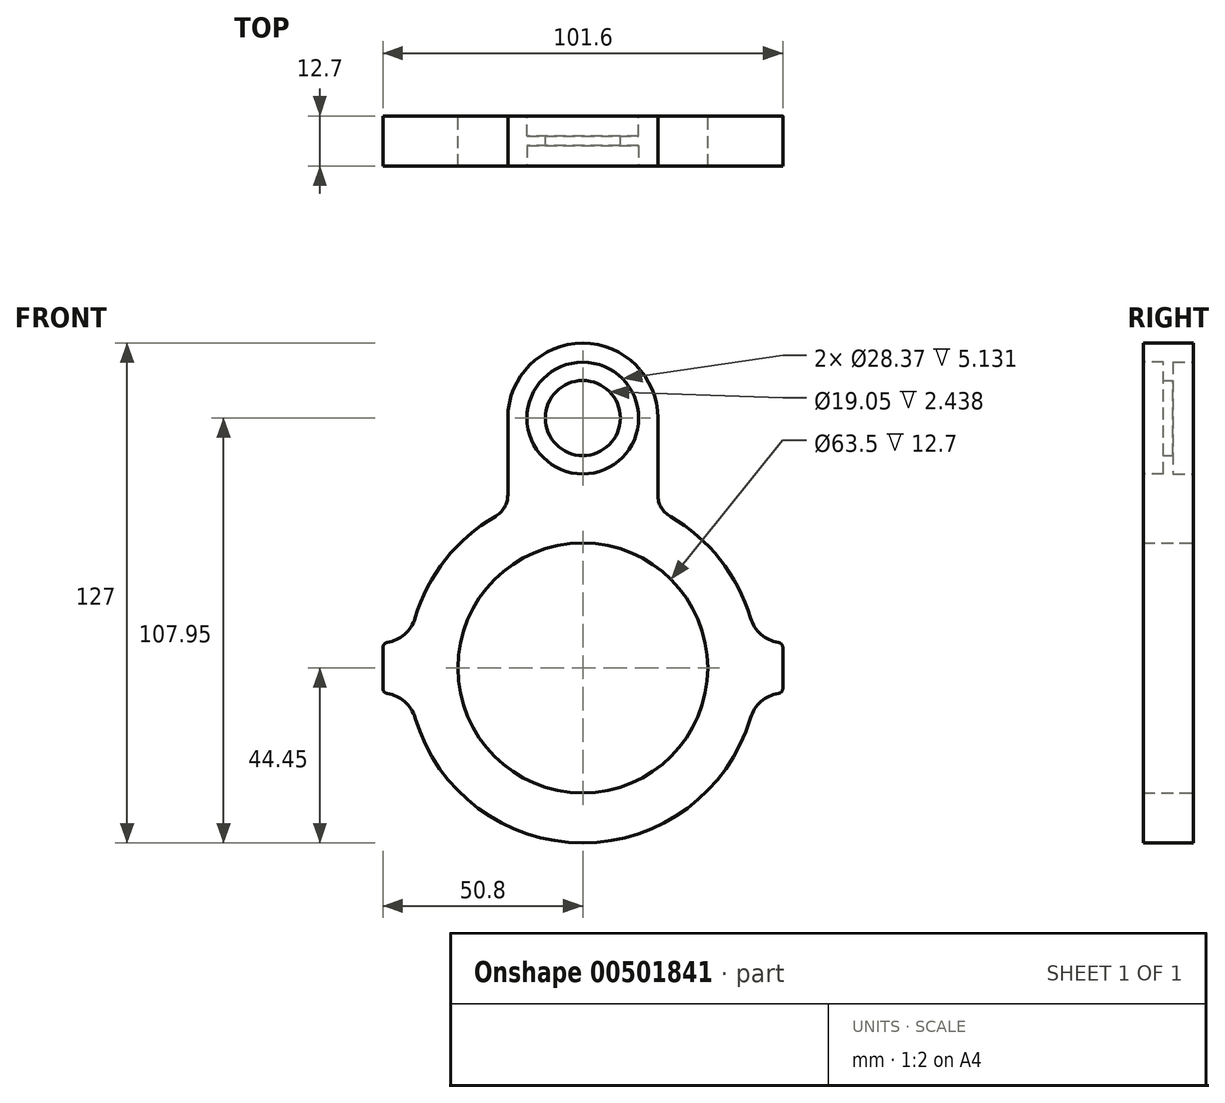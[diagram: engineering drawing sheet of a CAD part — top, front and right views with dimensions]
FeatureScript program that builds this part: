
annotation { "Feature Type Name" : "Feature", "Feature Type Description" : "" }
export const myFeature = defineFeature(function(context is Context, id is Id, definition is map)
    precondition{}
    {
        {
            var Q0;
            Q0=qCreatedBy(makeId("Front.planeOp"),FACE);
            var sketch = newSketch(context, id + "F0", { "sketchPlane" : qUnion([Q0])});
            skLineSegment(sketch, "E0", {"start": v(0, 0) * mm, "end": v(0, -31.75) * mm, "construction": true});
            skLineSegment(sketch, "E1", {"start": v(0, 0) * mm, "end": v(0, 31.75) * mm, "construction": true});
            skCircle(sketch, "E2", {"center": v(0, -31.75) * mm, "radius": 31.75 * mm});
            skCircle(sketch, "E3", {"center": v(0, 31.75) * mm, "radius": 9.53 * mm});
            skArc(sketch, "E4", {"start": v(19.05, 31.75) * mm, "mid": v(0, 50.8) * mm, "end": v(-19.05, 31.75) * mm});
            skArc(sketch, "E5", {"start": v(-35.77, -5.36) * mm, "mid": v(-41.12, -14.87) * mm, "end": v(-44, -25.4) * mm});
            skPoint(sketch, "E6.start.orphan", {"position": v(-44.45, -31.75) * mm});
            skLineSegment(sketch, "E7", {"start": v(0, -31.75) * mm, "end": v(31.75, -31.75) * mm, "construction": true});
            skLineSegment(sketch, "E8", {"start": v(0, -31.75) * mm, "end": v(-50.8, -31.75) * mm, "construction": true});
            skLineSegment(sketch, "E9", {"start": v(-50.8, -25.4) * mm, "end": v(-44, -25.4) * mm});
            skLineSegment(sketch, "E10", {"start": v(-50.8, -38.1) * mm, "end": v(-44, -38.1) * mm});
            skLineSegment(sketch, "E11.trimOffspring", {"start": v(44, -38.1) * mm, "end": v(50.8, -38.1) * mm});
            skLineSegment(sketch, "E12.trimOffspring", {"start": v(44, -25.4) * mm, "end": v(50.8, -25.4) * mm});
            skLineSegment(sketch, "E13", {"start": v(-50.8, -25.4) * mm, "end": v(-50.8, -38.1) * mm});
            skLineSegment(sketch, "E14", {"start": v(50.8, -25.4) * mm, "end": v(50.8, -38.1) * mm});
            skArc(sketch, "E15.trimOffspring", {"start": v(-44, -38.1) * mm, "mid": v(0, -76.2) * mm, "end": v(44, -38.1) * mm});
            skArc(sketch, "E16.trimOffspring", {"start": v(44, -25.4) * mm, "mid": v(41.12, -14.87) * mm, "end": v(35.77, -5.36) * mm});
            skPoint(sketch, "E17.trimOffspring.end.orphan", {"position": v(50.8, -31.75) * mm});
            skPoint(sketch, "E18.MirrorCS.end.orphan", {"position": v(19.05, 31.75) * mm});
            skPoint(sketch, "E18.MirrorCS.start.orphan", {"position": v(35.77, -5.36) * mm});
            skArc(sketch, "E19", {"start": v(35.77, -5.36) * mm, "mid": v(29.62, 1.4) * mm, "end": v(22.23, 6.74) * mm});
            skLineSegment(sketch, "E20", {"start": v(19.05, 31.75) * mm, "end": v(19.05, 12.24) * mm, "construction": true});
            skLineSegment(sketch, "E21", {"start": v(-19.05, 31.75) * mm, "end": v(-19.05, 12.24) * mm, "construction": true});
            skLineSegment(sketch, "E22", {"start": v(19.05, 12.7) * mm, "end": v(-19.05, 12.7) * mm, "construction": true});
            skLineSegment(sketch, "E23", {"start": v(19.05, 31.75) * mm, "end": v(19.05, 12.24) * mm});
            skLineSegment(sketch, "E24", {"start": v(-19.05, 31.75) * mm, "end": v(-19.05, 12.24) * mm});
            skArc(sketch, "E25.trimOffspring", {"start": v(-22.22, 6.74) * mm, "mid": v(-29.62, 1.4) * mm, "end": v(-35.77, -5.36) * mm});
            skPoint(sketch, "E26.newPointB", {"position": v(-19.05, -6.35) * mm});
            skArc(sketch, "E26.filletArc", {"start": v(-22.22, 6.74) * mm, "mid": v(-19.9, 9.07) * mm, "end": v(-19.05, 12.24) * mm});
            skPoint(sketch, "E27.newPointB", {"position": v(19.05, -6.35) * mm});
            skArc(sketch, "E27.filletArc", {"start": v(19.05, 12.24) * mm, "mid": v(19.9, 9.07) * mm, "end": v(22.22, 6.74) * mm});
            skSolve(sketch);
        }
        {
            var Q0;
            Q0 = qSketchRegion(id + "F0", true);
            extrude(context, id + "F1", {"entities" : qUnion([Q0]), "depth" : 12.7 * mm});
        }
        {
            var Q0;
            Q0=makeQuery(id+"F1.opExtrude","SWEPT_EDGE",EDGE,{"disambiguationData":[OSD([sQuery(id+"F0.wireOp",EDGE,"E5"),sQuery(id+"F0.wireOp",EDGE,"E9")])]});
            var Q1;
            Q1=makeQuery(id+"F1.opExtrude","SWEPT_EDGE",EDGE,{"disambiguationData":[OSD([sQuery(id+"F0.wireOp",EDGE,"E12.trimOffspring"),sQuery(id+"F0.wireOp",EDGE,"E16.trimOffspring")])]});
            var Q2;
            Q2=makeQuery(id+"F1.opExtrude","SWEPT_EDGE",EDGE,{"disambiguationData":[OSD([sQuery(id+"F0.wireOp",EDGE,"E10"),sQuery(id+"F0.wireOp",EDGE,"E15.trimOffspring")])]});
            var Q3;
            Q3=makeQuery(id+"F1.opExtrude","SWEPT_EDGE",EDGE,{"disambiguationData":[OSD([sQuery(id+"F0.wireOp",EDGE,"E11.trimOffspring"),sQuery(id+"F0.wireOp",EDGE,"E15.trimOffspring")])]});
            fillet(context, id + "F2", {"entities" : qUnion([Q0, Q1, Q2, Q3]), "radius" : 8.9 * mm, "tangentPropagation" : true, "allowEdgeOverflow" : false});
        }
        {
            var Q0;
            Q0=makeQuery(id+"F2.opFillet","BLEND_EDGE",EDGE,{"blendedFrom":[makeQuery(id+"F1.opExtrude","SWEPT_EDGE",EDGE,{"disambiguationData":[OSD([sQuery(id+"F0.wireOp",EDGE,"E5"),sQuery(id+"F0.wireOp",EDGE,"E9")])]}),makeQuery(id+"F1.opExtrude","SWEPT_FACE",FACE,{"disambiguationData":[OSD([sQuery(id+"F0.wireOp",EDGE,"E13")])]})],"blendedInto":[makeQuery(id+"F1.opExtrude","SWEPT_FACE",FACE,{"disambiguationData":[OSD([sQuery(id+"F0.wireOp",EDGE,"E13")])]})]});
            var Q1;
            Q1=makeQuery(id+"F2.opFillet","BLEND_EDGE",EDGE,{"blendedFrom":[makeQuery(id+"F1.opExtrude","SWEPT_EDGE",EDGE,{"disambiguationData":[OSD([sQuery(id+"F0.wireOp",EDGE,"E10"),sQuery(id+"F0.wireOp",EDGE,"E15.trimOffspring")])]}),makeQuery(id+"F1.opExtrude","SWEPT_FACE",FACE,{"disambiguationData":[OSD([sQuery(id+"F0.wireOp",EDGE,"E13")])]})],"blendedInto":[makeQuery(id+"F1.opExtrude","SWEPT_FACE",FACE,{"disambiguationData":[OSD([sQuery(id+"F0.wireOp",EDGE,"E13")])]})]});
            var Q2;
            Q2=makeQuery(id+"F2.opFillet","BLEND_EDGE",EDGE,{"blendedFrom":[makeQuery(id+"F1.opExtrude","SWEPT_EDGE",EDGE,{"disambiguationData":[OSD([sQuery(id+"F0.wireOp",EDGE,"E12.trimOffspring"),sQuery(id+"F0.wireOp",EDGE,"E16.trimOffspring")])]}),makeQuery(id+"F1.opExtrude","SWEPT_FACE",FACE,{"disambiguationData":[OSD([sQuery(id+"F0.wireOp",EDGE,"E14")])]})],"blendedInto":[makeQuery(id+"F1.opExtrude","SWEPT_FACE",FACE,{"disambiguationData":[OSD([sQuery(id+"F0.wireOp",EDGE,"E14")])]})]});
            var Q3;
            Q3=makeQuery(id+"F2.opFillet","BLEND_EDGE",EDGE,{"blendedFrom":[makeQuery(id+"F1.opExtrude","SWEPT_EDGE",EDGE,{"disambiguationData":[OSD([sQuery(id+"F0.wireOp",EDGE,"E11.trimOffspring"),sQuery(id+"F0.wireOp",EDGE,"E15.trimOffspring")])]}),makeQuery(id+"F1.opExtrude","SWEPT_FACE",FACE,{"disambiguationData":[OSD([sQuery(id+"F0.wireOp",EDGE,"E14")])]})],"blendedInto":[makeQuery(id+"F1.opExtrude","SWEPT_FACE",FACE,{"disambiguationData":[OSD([sQuery(id+"F0.wireOp",EDGE,"E14")])]})]});
            fillet(context, id + "F3", {"entities" : qUnion([Q0, Q1, Q2, Q3]), "radius" : 1.27 * mm, "tangentPropagation" : true, "allowEdgeOverflow" : false});
        }
        {
            var Q0;
            Q0=makeQuery(id+"F1.opExtrude","CAP_FACE",FACE,{"disambiguationData":[OSD([sQuery(id+"F0.wireOp",EDGE,"E2"),sQuery(id+"F0.wireOp",EDGE,"E3"),sQuery(id+"F0.wireOp",EDGE,"E4"),sQuery(id+"F0.wireOp",EDGE,"E5"),sQuery(id+"F0.wireOp",EDGE,"E9"),sQuery(id+"F0.wireOp",EDGE,"E10"),sQuery(id+"F0.wireOp",EDGE,"E11.trimOffspring"),sQuery(id+"F0.wireOp",EDGE,"E12.trimOffspring"),sQuery(id+"F0.wireOp",EDGE,"E13"),sQuery(id+"F0.wireOp",EDGE,"E14"),sQuery(id+"F0.wireOp",EDGE,"E15.trimOffspring"),sQuery(id+"F0.wireOp",EDGE,"E16.trimOffspring"),sQuery(id+"F0.wireOp",EDGE,"E19"),sQuery(id+"F0.wireOp",EDGE,"E23"),sQuery(id+"F0.wireOp",EDGE,"E24"),sQuery(id+"F0.wireOp",EDGE,"E25.trimOffspring"),sQuery(id+"F0.wireOp",EDGE,"E26.filletArc"),sQuery(id+"F0.wireOp",EDGE,"E27.filletArc")])],"isStart":false});
            var sketch = newSketch(context, id + "F4", { "sketchPlane" : qUnion([Q0])});
            skCircle(sketch, "E28", {"center": v(0, 31.75) * mm, "radius": 14.19 * mm});
            skSolve(sketch);
        }
        {
            var Q0;
            Q0=makeQuery(id+"F4.imprint","IMPRINT",FACE,{"disambiguationData":[TD([[makeQuery(id+"F4.imprint","IMPRINT",EDGE,{"derivedFrom":sQuery(id+"F4.wireOp",EDGE,"E28")}),1.0]])]});
            extrude(context, id + "F5", {"entities" : qUnion([Q0]), "operationType" : NewBodyOperationType.REMOVE, "oppositeDirection" : true, "depth" : 5.13 * mm});
        }
        {
            var Q0;
            Q0=makeQuery(id+"F1.opExtrude","CAP_FACE",FACE,{"disambiguationData":[OSD([sQuery(id+"F0.wireOp",EDGE,"E2"),sQuery(id+"F0.wireOp",EDGE,"E3"),sQuery(id+"F0.wireOp",EDGE,"E4"),sQuery(id+"F0.wireOp",EDGE,"E5"),sQuery(id+"F0.wireOp",EDGE,"E9"),sQuery(id+"F0.wireOp",EDGE,"E10"),sQuery(id+"F0.wireOp",EDGE,"E11.trimOffspring"),sQuery(id+"F0.wireOp",EDGE,"E12.trimOffspring"),sQuery(id+"F0.wireOp",EDGE,"E13"),sQuery(id+"F0.wireOp",EDGE,"E14"),sQuery(id+"F0.wireOp",EDGE,"E15.trimOffspring"),sQuery(id+"F0.wireOp",EDGE,"E16.trimOffspring"),sQuery(id+"F0.wireOp",EDGE,"E19"),sQuery(id+"F0.wireOp",EDGE,"E23"),sQuery(id+"F0.wireOp",EDGE,"E24"),sQuery(id+"F0.wireOp",EDGE,"E25.trimOffspring"),sQuery(id+"F0.wireOp",EDGE,"E26.filletArc"),sQuery(id+"F0.wireOp",EDGE,"E27.filletArc")])],"isStart":true});
            var sketch = newSketch(context, id + "F6", { "sketchPlane" : qUnion([Q0])});
            skCircle(sketch, "E29", {"center": v(0, 31.75) * mm, "radius": 14.19 * mm});
            skSolve(sketch);
        }
        {
            var Q0;
            Q0=makeQuery(id+"F6.imprint","IMPRINT",FACE,{"disambiguationData":[TD([[makeQuery(id+"F6.imprint","IMPRINT",EDGE,{"derivedFrom":sQuery(id+"F6.wireOp",EDGE,"E29")}),1.0]])]});
            extrude(context, id + "F7", {"entities" : qUnion([Q0]), "operationType" : NewBodyOperationType.REMOVE, "oppositeDirection" : true, "depth" : 5.13 * mm});
        }
    });
